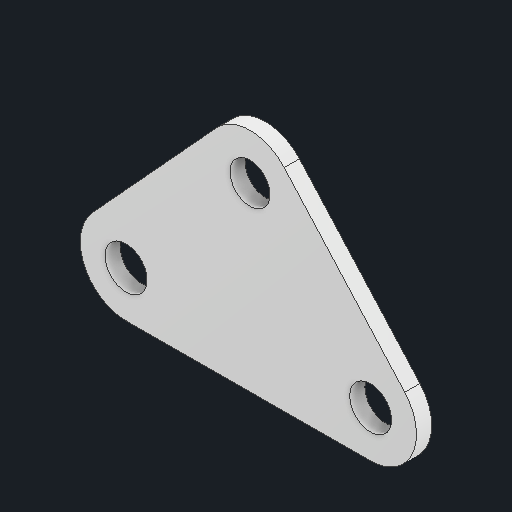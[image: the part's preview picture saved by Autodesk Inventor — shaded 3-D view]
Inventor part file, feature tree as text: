
AUTODESK INVENTOR PART (.ipt)
format: ipt  version: 2025 (Build 290162000, 162)  size: 113,664 bytes
history: native  units: in
note: dims shown in document units (in); Inventor stores cm internally (conversion verified against a paired STEP export)
features: other x3, extrude x1, sketch x1
ambient origin geometry x8: Origin, YZ Plane, XZ Plane, XY Plane, X Axis, Y Axis, Z Axis, Center Point
bodies: Solid1 (feature_tree)
feature tree (5):
  other  "Blocks"
  extrude  "Extrusion1"  Depth=0.0625in
  sketch  "Sketch1"  dims[d0=0.164in d1=0.375in d2=0.375in d3=0.375in d4=0.0625in d5=0.0in]
  other  "main"
  other  "main:1"
